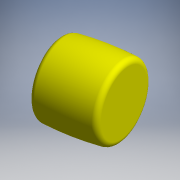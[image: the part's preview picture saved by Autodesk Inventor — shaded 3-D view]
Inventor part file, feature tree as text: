
AUTODESK INVENTOR PART (.ipt)
format: ipt  version: 2017.3 (Build 213256000, 256)  size: 129,024 bytes
history: native  units: mm (DEFAULTED — no unit token found)
features: other x14, revolve x1, sketch x1
ambient origin geometry x8: Origin, YZ Plane, XZ Plane, XY Plane, X Axis, Y Axis, Z Axis, Center Point
bodies: Solid1 (feature_tree)
feature tree (16):
  revolve  "Revolution1"  [1 undecoded]
  other  "NO_GEO_XY"
  other  "NO_GEO_YZ"
  other  "NO_GEO_ZX"
  other  "NO_GEO_X"
  other  "NO_GEO_Y"
  other  "NO_GEO_Z"
  other  "NO_GEO_Center"
  other  "roller2_XY"
  other  "roller2_YZ"
  other  "roller2_ZX"
  other  "roller2_X"
  other  "roller2_Y"
  other  "roller2_Z"
  other  "roller2_Center"
  sketch  "Sketch_1"  dims[d0=360.0deg]
note: 1 required parameter value undecoded (feature->parameter linkage not recoverable at this tier; creation-order binding heuristic only, values carry confidence <= 0.55)
